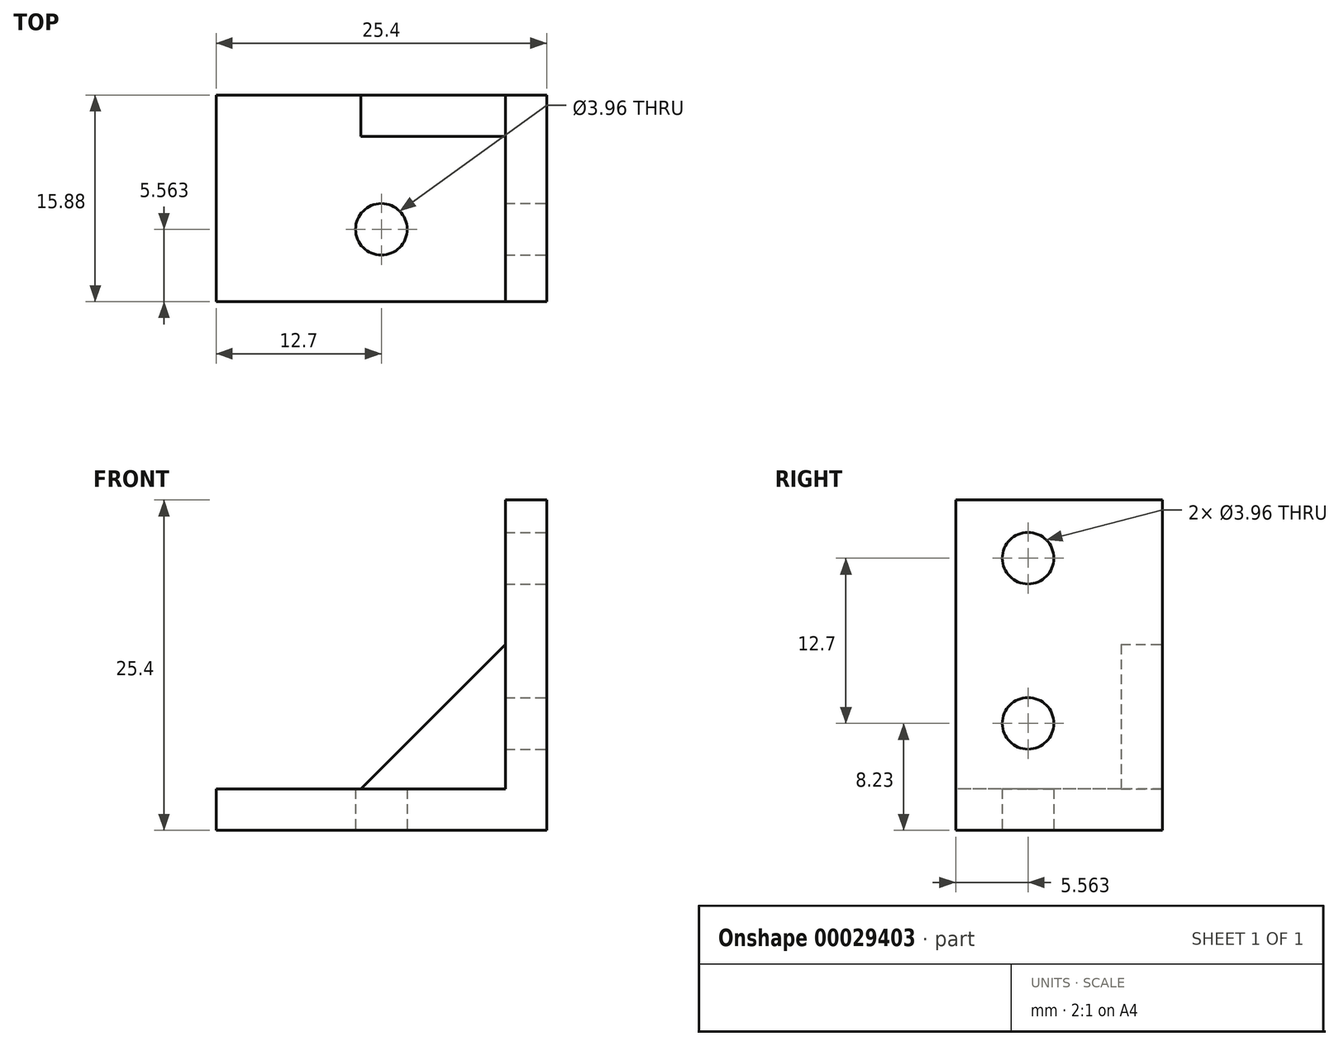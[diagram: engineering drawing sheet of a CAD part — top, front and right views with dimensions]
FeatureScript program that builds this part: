
annotation { "Feature Type Name" : "Feature", "Feature Type Description" : "" }
export const myFeature = defineFeature(function(context is Context, id is Id, definition is map)
    precondition{}
    {
        {
            var Q0;
            Q0=qCreatedBy(makeId("Front.planeOp"),FACE);
            var sketch = newSketch(context, id + "F0", { "sketchPlane" : qUnion([Q0])});
            skLineSegment(sketch, "E0.bottom", {"start": v(-12.7, 3.17) * mm, "end": v(9.53, 3.18) * mm});
            skLineSegment(sketch, "E0.top", {"start": v(-12.7, 0) * mm, "end": v(12.7, 0) * mm});
            skLineSegment(sketch, "E0.left", {"start": v(-12.7, 3.17) * mm, "end": v(-12.7, 0) * mm});
            skLineSegment(sketch, "E0.right", {"start": v(12.7, 3.17) * mm, "end": v(12.7, 0) * mm});
            skLineSegment(sketch, "E1", {"start": v(12.7, 25.4) * mm, "end": v(12.7, 0) * mm});
            skLineSegment(sketch, "E2", {"start": v(12.7, 25.4) * mm, "end": v(9.53, 25.4) * mm});
            skLineSegment(sketch, "E3", {"start": v(9.53, 25.4) * mm, "end": v(9.53, 3.17) * mm});
            skLineSegment(sketch, "E4", {"start": v(9.53, 14.29) * mm, "end": v(-1.59, 3.17) * mm});
            skSolve(sketch);
        }
        {
            var Q0;
            {var subQ5=sQuery(id+"F0.wireOp",EDGE,"E0.top");Q0=makeQuery(id+"F0.imprint","IMPRINT",FACE,{"disambiguationData":[TD([[makeQuery(id+"F0.imprint","IMPRINT",EDGE,{"derivedFrom":subQ5}),1.0]])]});}
            extrude(context, id + "F1", {"entities" : qUnion([Q0]), "oppositeDirection" : true, "depth" : 15.88 * mm});
        }
        {
            var Q0;
            Q0=makeQuery(id+"F1.opExtrude","SWEPT_FACE",FACE,{"disambiguationData":[OSD([sQuery(id+"F0.wireOp",EDGE,"E1")])]});
            var sketch = newSketch(context, id + "F2", { "sketchPlane" : qUnion([Q0])});
            skCircle(sketch, "E5", {"center": v(5.56, 20.93) * mm, "radius": 1.98 * mm});
            skCircle(sketch, "E6", {"center": v(5.56, 8.23) * mm, "radius": 1.98 * mm});
            skSolve(sketch);
        }
        {
            var Q0;
            Q0=makeQuery(id+"F2.imprint","IMPRINT",FACE,{"disambiguationData":[TD([[makeQuery(id+"F2.imprint","IMPRINT",EDGE,{"derivedFrom":sQuery(id+"F2.wireOp",EDGE,"E5")}),1.0]])]});
            var Q1;
            Q1=makeQuery(id+"F2.imprint","IMPRINT",FACE,{"disambiguationData":[TD([[makeQuery(id+"F2.imprint","IMPRINT",EDGE,{"derivedFrom":sQuery(id+"F2.wireOp",EDGE,"E6")}),1.0]])]});
            extrude(context, id + "F3", {"entities" : qUnion([Q0, Q1]), "operationType" : NewBodyOperationType.REMOVE, "oppositeDirection" : true, "depth" : 25.4 * mm});
        }
        {
            var Q0;
            Q0=makeQuery(id+"F1.opExtrude","CAP_FACE",FACE,{"disambiguationData":[OSD([sQuery(id+"F0.wireOp",EDGE,"E0.bottom"),sQuery(id+"F0.wireOp",EDGE,"E0.top"),sQuery(id+"F0.wireOp",EDGE,"E0.left"),sQuery(id+"F0.wireOp",EDGE,"E1"),sQuery(id+"F0.wireOp",EDGE,"E2"),sQuery(id+"F0.wireOp",EDGE,"E3")])],"isStart":false});
            var sketch = newSketch(context, id + "F4", { "sketchPlane" : qUnion([Q0])});
            skLineSegment(sketch, "E7", {"start": v(-9.53, 14.29) * mm, "end": v(1.59, 3.18) * mm});
            skSolve(sketch);
        }
        {
            var Q0;
            {var subQ1=sQuery(id+"F4.wireOp",EDGE,"E7");Q0=makeQuery(id+"F4.imprint","IMPRINT",FACE,{"disambiguationData":[TD([[makeQuery(id+"F4.imprint","IMPRINT",EDGE,{"derivedFrom":subQ1}),-1.0]])]});}
            extrude(context, id + "F5", {"entities" : qUnion([Q0]), "operationType" : NewBodyOperationType.ADD, "oppositeDirection" : true, "depth" : 3.17 * mm});
        }
        {
            var Q0;
            Q0=makeQuery(id+"F1.opExtrude","SWEPT_FACE",FACE,{"disambiguationData":[OSD([sQuery(id+"F0.wireOp",EDGE,"E0.top")])]});
            var sketch = newSketch(context, id + "F6", { "sketchPlane" : qUnion([Q0])});
            skCircle(sketch, "E8", {"center": v(0, -5.56) * mm, "radius": 1.98 * mm});
            skSolve(sketch);
        }
        {
            var Q0;
            Q0=makeQuery(id+"F6.imprint","IMPRINT",FACE,{"disambiguationData":[TD([[makeQuery(id+"F6.imprint","IMPRINT",EDGE,{"derivedFrom":sQuery(id+"F6.wireOp",EDGE,"E8")}),1.0]])]});
            extrude(context, id + "F7", {"entities" : qUnion([Q0]), "operationType" : NewBodyOperationType.REMOVE, "oppositeDirection" : true, "depth" : 25.4 * mm});
        }
    });
